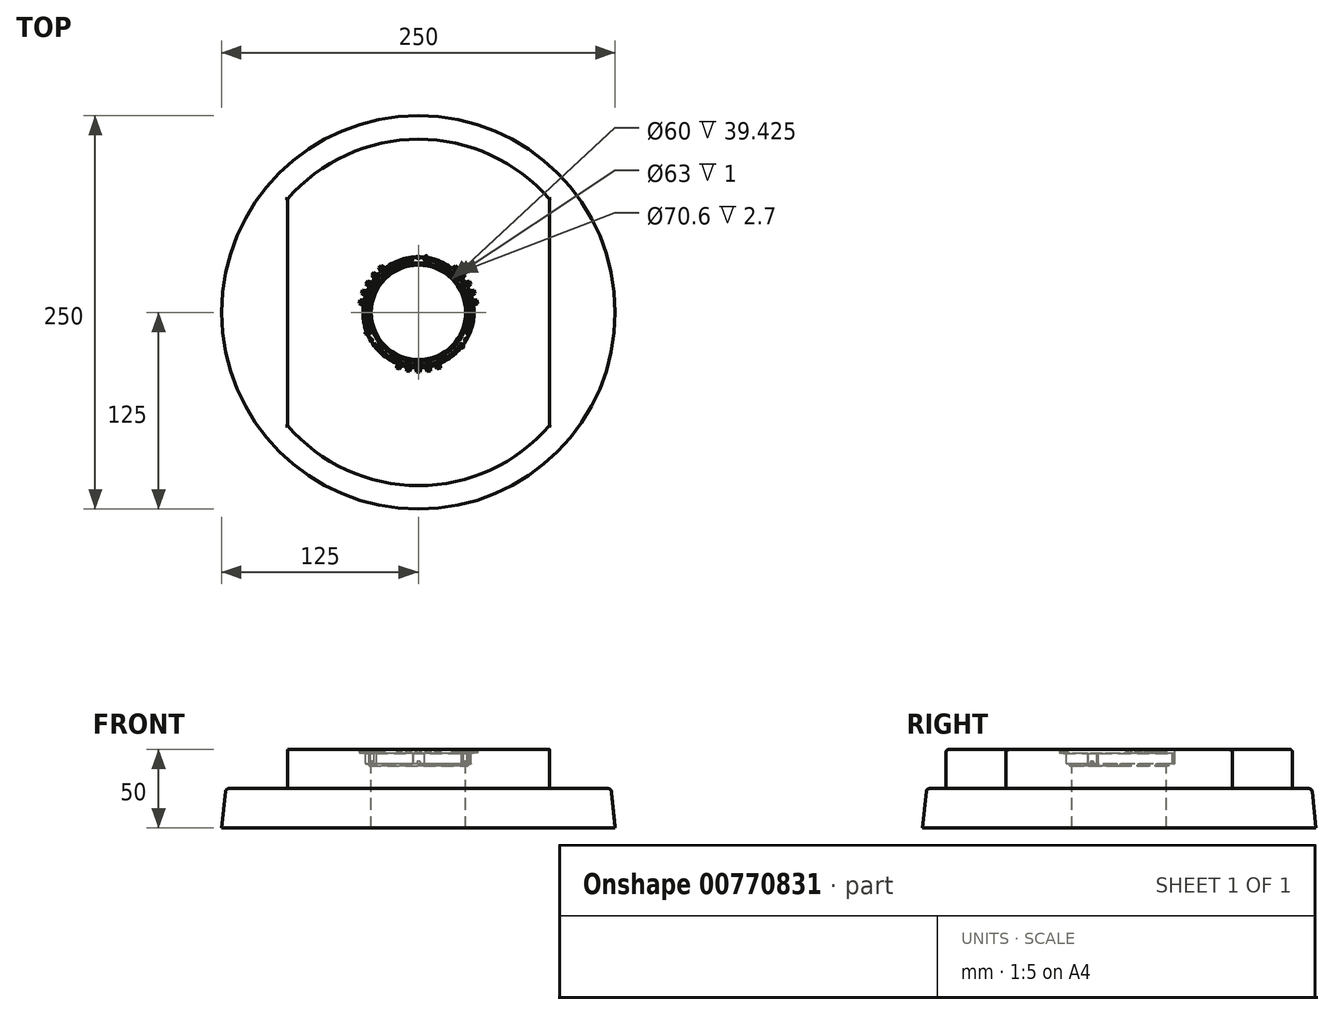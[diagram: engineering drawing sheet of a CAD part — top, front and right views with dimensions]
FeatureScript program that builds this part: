
annotation { "Feature Type Name" : "Feature", "Feature Type Description" : "" }
export const myFeature = defineFeature(function(context is Context, id is Id, definition is map)
    precondition{}
    {
        {
            var Q0;
            Q0=qCreatedBy(makeId("Front.planeOp"),FACE);
            var sketch = newSketch(context, id + "F0", { "sketchPlane" : qUnion([Q0])});
            skLineSegment(sketch, "E0", {"start": v(0, 117.97) * mm, "end": v(0, 0) * mm, "construction": true});
            skLineSegment(sketch, "E1", {"start": v(0, 0) * mm, "end": v(-164.87, 0) * mm, "construction": true});
            skLineSegment(sketch, "E2.bottom", {"start": v(-125, 0) * mm, "end": v(-30, 0) * mm});
            skLineSegment(sketch, "E2.top", {"start": v(-110, 50) * mm, "end": v(-37.95, 50) * mm});
            skLineSegment(sketch, "E2.right", {"start": v(0, 0) * mm, "end": v(0, 50) * mm});
            skLineSegment(sketch, "E3", {"start": v(-125, 25) * mm, "end": v(-110, 25) * mm});
            skLineSegment(sketch, "E4", {"start": v(-110, 25) * mm, "end": v(-110, 50) * mm});
            skLineSegment(sketch, "E5", {"start": v(-30, 39.43) * mm, "end": v(-30, 0) * mm});
            skLineSegment(sketch, "E6", {"start": v(-33.5, 46.85) * mm, "end": v(-33.5, 40.73) * mm});
            skLineSegment(sketch, "E7", {"start": v(-33.5, 40.73) * mm, "end": v(-31.5, 40.73) * mm});
            skLineSegment(sketch, "E8", {"start": v(-31.5, 40.73) * mm, "end": v(-31.5, 39.43) * mm});
            skLineSegment(sketch, "E9", {"start": v(-31.5, 39.43) * mm, "end": v(-30, 39.43) * mm});
            skPoint(sketch, "E10.orphan", {"position": v(-30, 50) * mm});
            skLineSegment(sketch, "E11", {"start": v(-33.5, 46.85) * mm, "end": v(-33.5, 50) * mm});
            skLineSegment(sketch, "E12", {"start": v(-33.5, 50) * mm, "end": v(-37.95, 50) * mm});
            skLineSegment(sketch, "E13", {"start": v(-125, 0) * mm, "end": v(-125, 25) * mm});
            skLineSegment(sketch, "E14", {"start": v(-125, 0) * mm, "end": v(-122.32, 25) * mm});
            skSolve(sketch);
        }
        {
            var Q0;
            Q0=makeQuery(id+"F0.imprint","IMPRINT",FACE,{"disambiguationData":[TD([[makeQuery(id+"F0.imprint","IMPRINT",EDGE,{"derivedFrom":sQuery(id+"F0.wireOp",EDGE,"E2.bottom")}),1.0]])]});
            var Q1;
            Q1=sQuery(id+"F0.wireOp",EDGE,"E0");
            revolve(context, id + "F1", {"surfaceOperationType" : NewSurfaceOperationType.NEW, "entities" : qUnion([Q0]), "axis" : qUnion([Q1]), "revolveType" : RevolveType.FULL});
        }
        {
            var Q0;
            Q0=makeQuery(id+"F1.opRevolve","SWEPT_FACE",FACE,{"disambiguationData":[OSD([sQuery(id+"F0.wireOp",EDGE,"E2.top"),sQuery(id+"F0.wireOp",EDGE,"E12")])]});
            var sketch = newSketch(context, id + "F2", { "sketchPlane" : qUnion([Q0])});
            skLineSegment(sketch, "E15.bottom", {"start": v(-83.23, 71.92) * mm, "end": v(83.23, 71.92) * mm});
            skLineSegment(sketch, "E15.top", {"start": v(-83.23, -71.92) * mm, "end": v(83.23, -71.92) * mm});
            skLineSegment(sketch, "E15.left", {"start": v(-83.23, 71.92) * mm, "end": v(-83.23, -71.92) * mm});
            skLineSegment(sketch, "E15.right", {"start": v(83.23, 71.92) * mm, "end": v(83.23, -71.92) * mm});
            skPoint(sketch, "E15.middle", {"position": v(0, 0) * mm});
            skCircle(sketch, "E16", {"center": v(0, 0) * mm, "radius": 110 * mm});
            skSolve(sketch);
        }
        {
            var Q0;
            {var subQ0=sQuery(id+"F2.wireOp",EDGE,"E15.right");Q0=makeQuery(id+"F2.imprint","IMPRINT",FACE,{"disambiguationData":[TD([[makeQuery(id+"F2.imprint","IMPRINT",EDGE,{"derivedFrom":subQ0}),1.0]])]});}
            var Q1;
            {var subQ0=sQuery(id+"F2.wireOp",EDGE,"E15.left");Q1=makeQuery(id+"F2.imprint","IMPRINT",FACE,{"disambiguationData":[TD([[makeQuery(id+"F2.imprint","IMPRINT",EDGE,{"derivedFrom":subQ0}),-1.0]])]});}
            extrude(context, id + "F3", {"entities" : qUnion([Q0, Q1]), "operationType" : NewBodyOperationType.REMOVE, "oppositeDirection" : true, "depth" : 25 * mm, "offsetDistance" : 25 * mm});
        }
        {
            var Q0;
            Q0=makeQuery(id+"F3.boolean.opBoolean","SPLIT",EDGE,{"disambiguationData":[OD(1.0)],"derivedFrom":makeQuery(id+"F1.opRevolve","SWEPT_EDGE",EDGE,{"disambiguationData":[OSD([sQuery(id+"F0.wireOp",EDGE,"E2.top"),sQuery(id+"F0.wireOp",EDGE,"E4")])]})});
            var Q1;
            Q1=makeQuery(id+"F3.boolean.opBoolean","COPY",EDGE,{"derivedFrom":makeQuery(id+"F3.opExtrude","CAP_EDGE",EDGE,{"disambiguationData":[OSD([sQuery(id+"F2.wireOp",EDGE,"E15.left")])],"isStart":true})});
            var Q2;
            Q2=makeQuery(id+"F3.boolean.opBoolean","SPLIT",EDGE,{"disambiguationData":[OD(0.0)],"derivedFrom":makeQuery(id+"F1.opRevolve","SWEPT_EDGE",EDGE,{"disambiguationData":[OSD([sQuery(id+"F0.wireOp",EDGE,"E2.top"),sQuery(id+"F0.wireOp",EDGE,"E4")])]})});
            var Q3;
            Q3=makeQuery(id+"F3.boolean.opBoolean","COPY",EDGE,{"derivedFrom":makeQuery(id+"F3.opExtrude","CAP_EDGE",EDGE,{"disambiguationData":[OSD([sQuery(id+"F2.wireOp",EDGE,"E15.right")])],"isStart":true})});
            var Q4;
            Q4=makeQuery(id+"F1.opRevolve","SWEPT_EDGE",EDGE,{"disambiguationData":[OSD([sQuery(id+"F0.wireOp",EDGE,"E3"),sQuery(id+"F0.wireOp",EDGE,"E14")])]});
            fillet(context, id + "F4", {"entities" : qUnion([Q0, Q1, Q2, Q3, Q4]), "radius" : 2 * mm, "tangentPropagation" : true, "allowEdgeOverflow" : false});
        }
        {
            var Q0;
            Q0=makeQuery(id+"F3.boolean.opBoolean","COPY",EDGE,{"derivedFrom":makeQuery(id+"F3.opExtrude","CAP_EDGE",EDGE,{"disambiguationData":[OSD([sQuery(id+"F2.wireOp",EDGE,"E15.left")])],"isStart":false})});
            var Q1;
            Q1=makeQuery(id+"F3.boolean.opBoolean","COPY",EDGE,{"derivedFrom":makeQuery(id+"F3.opExtrude","CAP_EDGE",EDGE,{"disambiguationData":[OSD([sQuery(id+"F2.wireOp",EDGE,"E15.right")])],"isStart":false})});
            var Q2;
            Q2=makeQuery(id+"F3.boolean.opBoolean","SPLIT",EDGE,{"disambiguationData":[OD(0.0)],"derivedFrom":makeQuery(id+"F1.opRevolve","SWEPT_EDGE",EDGE,{"disambiguationData":[OSD([sQuery(id+"F0.wireOp",EDGE,"E3"),sQuery(id+"F0.wireOp",EDGE,"E4")])]})});
            var Q3;
            Q3=makeQuery(id+"F3.boolean.opBoolean","SPLIT",EDGE,{"disambiguationData":[OD(1.0)],"derivedFrom":makeQuery(id+"F1.opRevolve","SWEPT_EDGE",EDGE,{"disambiguationData":[OSD([sQuery(id+"F0.wireOp",EDGE,"E3"),sQuery(id+"F0.wireOp",EDGE,"E4")])]})});
            fillet(context, id + "F5", {"entities" : qUnion([Q0, Q1, Q2, Q3]), "radius" : 1 * mm, "tangentPropagation" : true, "allowEdgeOverflow" : false});
        }
        {
            var Q0;
            Q0=makeQuery(id+"F1.opRevolve","SWEPT_EDGE",EDGE,{"disambiguationData":[OSD([sQuery(id+"F0.wireOp",EDGE,"E8"),sQuery(id+"F0.wireOp",EDGE,"E9")])]});
            fillet(context, id + "F6", {"entities" : qUnion([Q0]), "radius" : .3 * mm, "tangentPropagation" : true, "allowEdgeOverflow" : false});
        }
        {
            var Q0;
            Q0=qCreatedBy(makeId("Front.planeOp"),FACE);
            cPlane(context, id + "F7", {"entities" : qUnion([Q0]), "cplaneType" : CPlaneType.OFFSET, "offset" : 30 * mm, "width" : 150 * mm, "height" : 150 * mm});
        }
        {
            var Q0;
            Q0=qCreatedBy(makeId("Front.planeOp"),FACE);
            cPlane(context, id + "F8", {"entities" : qUnion([Q0]), "cplaneType" : CPlaneType.OFFSET, "offset" : 38 * mm, "width" : 150 * mm, "height" : 150 * mm});
        }
        {
            var Q0;
            Q0=qCreatedBy(id+"F8.planeOp",FACE);
            var sketch = newSketch(context, id + "F9", { "sketchPlane" : qUnion([Q0])});
            skPoint(sketch, "E17.start.orphan", {"position": v(0, 93.3) * mm});
            skLineSegment(sketch, "E18", {"start": v(0, 50) * mm, "end": v(-1.1, 50) * mm});
            skLineSegment(sketch, "E19", {"start": v(0, 100.28) * mm, "end": v(0, 50) * mm, "construction": true});
            skLineSegment(sketch, "E20.MirrorCS", {"start": v(0, 50) * mm, "end": v(1.1, 50) * mm});
            skPoint(sketch, "E21", {"position": v(0, 47.8) * mm});
            skLineSegment(sketch, "E22", {"start": v(-1.1, 50) * mm, "end": v(-1.1, 48.2) * mm});
            skLineSegment(sketch, "E23", {"start": v(-1.1, 48.2) * mm, "end": v(0, 47.8) * mm});
            skLineSegment(sketch, "E24.MirrorCS", {"start": v(1.1, 50) * mm, "end": v(1.1, 48.2) * mm});
            skLineSegment(sketch, "E25.MirrorCS", {"start": v(1.1, 48.2) * mm, "end": v(0, 47.8) * mm});
            skLineSegment(sketch, "E26.trimOffspring", {"start": v(0, 47.8) * mm, "end": v(0, 0) * mm, "construction": true});
            skSolve(sketch);
        }
        {
            var Q0;
            Q0=qCreatedBy(id+"F7.planeOp",FACE);
            var sketch = newSketch(context, id + "F10", { "sketchPlane" : qUnion([Q0])});
            skLineSegment(sketch, "E27", {"start": v(0, 52.95) * mm, "end": v(0, 0) * mm, "construction": true});
            skLineSegment(sketch, "E28", {"start": v(-3, 50) * mm, "end": v(0, 50) * mm});
            skLineSegment(sketch, "E29.MirrorCS", {"start": v(3, 50) * mm, "end": v(0, 50) * mm});
            skLineSegment(sketch, "E30", {"start": v(-3, 50) * mm, "end": v(-3, 48.2) * mm});
            skPoint(sketch, "E31", {"position": v(0, 47.2) * mm});
            skLineSegment(sketch, "E32", {"start": v(-3, 48.2) * mm, "end": v(0, 47.2) * mm});
            skLineSegment(sketch, "E33.MirrorCS", {"start": v(3, 50) * mm, "end": v(3, 48.2) * mm});
            skLineSegment(sketch, "E34.MirrorCS", {"start": v(3, 48.2) * mm, "end": v(0, 47.2) * mm});
            skSolve(sketch);
        }
        {
            var Q0;
            Q0=makeQuery(id+"F9.imprint","IMPRINT",FACE,{"disambiguationData":[TD([[makeQuery(id+"F9.imprint","IMPRINT",EDGE,{"derivedFrom":sQuery(id+"F9.wireOp",EDGE,"E18")}),1.0]])]});
            var Q1;
            Q1=makeQuery(id+"F10.imprint","IMPRINT",FACE,{"disambiguationData":[TD([[makeQuery(id+"F10.imprint","IMPRINT",EDGE,{"derivedFrom":sQuery(id+"F10.wireOp",EDGE,"E28")}),-1.0]])]});
            loft(context, id + "F11", {"operationType" : NewBodyOperationType.REMOVE, "sheetProfilesArray" : [{ "sheetProfileEntities" : qUnion([Q0]) }, { "sheetProfileEntities" : qUnion([Q1]) }]});
        }
        {
            var Q0;
            Q0=makeQuery(id+"F11.boolean.opBoolean","COPY",FACE,{"derivedFrom":makeQuery(id+"F11.opLoft","SWEPT_FACE",FACE,{"disambiguationData":[OSD([sQuery(id+"F9.wireOp",EDGE,"E22"),sQuery(id+"F9.wireOp",EDGE,"E23"),sQuery(id+"F9.wireOp",EDGE,"E25.MirrorCS"),sQuery(id+"F10.wireOp",EDGE,"E30"),sQuery(id+"F10.wireOp",EDGE,"E32"),sQuery(id+"F10.wireOp",EDGE,"E34.MirrorCS")])]})});
            var Q1;
            Q1=makeQuery(id+"F11.boolean.opBoolean","COPY",FACE,{"derivedFrom":makeQuery(id+"F11.opLoft","SWEPT_FACE",FACE,{"disambiguationData":[OSD([sQuery(id+"F9.wireOp",EDGE,"E18"),sQuery(id+"F9.wireOp",EDGE,"E22"),sQuery(id+"F9.wireOp",EDGE,"E23"),sQuery(id+"F10.wireOp",EDGE,"E28"),sQuery(id+"F10.wireOp",EDGE,"E30"),sQuery(id+"F10.wireOp",EDGE,"E32")])]})});
            var Q2;
            Q2=makeQuery(id+"F11.boolean.opBoolean","COPY",FACE,{"derivedFrom":makeQuery(id+"F11.opLoft","SWEPT_FACE",FACE,{"disambiguationData":[OSD([sQuery(id+"F9.wireOp",EDGE,"E23"),sQuery(id+"F9.wireOp",EDGE,"E24.MirrorCS"),sQuery(id+"F9.wireOp",EDGE,"E25.MirrorCS"),sQuery(id+"F10.wireOp",EDGE,"E32"),sQuery(id+"F10.wireOp",EDGE,"E33.MirrorCS"),sQuery(id+"F10.wireOp",EDGE,"E34.MirrorCS")])]})});
            var Q3;
            Q3=makeQuery(id+"F11.boolean.opBoolean","COPY",FACE,{"derivedFrom":makeQuery(id+"F11.opLoft","SWEPT_FACE",FACE,{"disambiguationData":[OSD([sQuery(id+"F9.wireOp",EDGE,"E24.MirrorCS"),sQuery(id+"F9.wireOp",EDGE,"E20.MirrorCS"),sQuery(id+"F9.wireOp",EDGE,"E25.MirrorCS"),sQuery(id+"F10.wireOp",EDGE,"E29.MirrorCS"),sQuery(id+"F10.wireOp",EDGE,"E33.MirrorCS"),sQuery(id+"F10.wireOp",EDGE,"E34.MirrorCS")])]})});
            var Q4;
            Q4=makeQuery(id+"F11.boolean.opBoolean","COPY",FACE,{"derivedFrom":makeQuery(id+"F11.opLoft","CAP_FACE",FACE,{"disambiguationData":[OSD([makeQuery(id+"F9.imprint","IMPRINT",FACE,{"disambiguationData":[TD([[makeQuery(id+"F9.imprint","IMPRINT",EDGE,{"derivedFrom":sQuery(id+"F9.wireOp",EDGE,"E18")}),1.0]])]})])],"isStart":true})});
            var Q5;
            Q5=makeQuery(id+"F1.opRevolve","SWEPT_FACE",FACE,{"disambiguationData":[OSD([sQuery(id+"F0.wireOp",EDGE,"E6"),sQuery(id+"F0.wireOp",EDGE,"E11")])]});
            circularPattern(context, id + "F12", {"patternType" : PatternType.FACE, "faces" : qUnion([Q0, Q1, Q2, Q3, Q4]), "axis" : qUnion([Q5]), "angle" : 20 * degree, "instanceCount" : 3, "equalSpace" : true});
        }
        {
            var Q0;
            Q0=makeQuery(id+"F11.boolean.opBoolean","COPY",FACE,{"derivedFrom":makeQuery(id+"F11.opLoft","SWEPT_FACE",FACE,{"disambiguationData":[OSD([sQuery(id+"F9.wireOp",EDGE,"E22"),sQuery(id+"F9.wireOp",EDGE,"E23"),sQuery(id+"F9.wireOp",EDGE,"E25.MirrorCS"),sQuery(id+"F10.wireOp",EDGE,"E30"),sQuery(id+"F10.wireOp",EDGE,"E32"),sQuery(id+"F10.wireOp",EDGE,"E34.MirrorCS")])]})});
            var Q1;
            Q1=makeQuery(id+"F11.boolean.opBoolean","COPY",FACE,{"derivedFrom":makeQuery(id+"F11.opLoft","SWEPT_FACE",FACE,{"disambiguationData":[OSD([sQuery(id+"F9.wireOp",EDGE,"E18"),sQuery(id+"F9.wireOp",EDGE,"E22"),sQuery(id+"F9.wireOp",EDGE,"E23"),sQuery(id+"F10.wireOp",EDGE,"E28"),sQuery(id+"F10.wireOp",EDGE,"E30"),sQuery(id+"F10.wireOp",EDGE,"E32")])]})});
            var Q2;
            Q2=makeQuery(id+"F11.boolean.opBoolean","COPY",FACE,{"derivedFrom":makeQuery(id+"F11.opLoft","SWEPT_FACE",FACE,{"disambiguationData":[OSD([sQuery(id+"F9.wireOp",EDGE,"E23"),sQuery(id+"F9.wireOp",EDGE,"E24.MirrorCS"),sQuery(id+"F9.wireOp",EDGE,"E25.MirrorCS"),sQuery(id+"F10.wireOp",EDGE,"E32"),sQuery(id+"F10.wireOp",EDGE,"E33.MirrorCS"),sQuery(id+"F10.wireOp",EDGE,"E34.MirrorCS")])]})});
            var Q3;
            Q3=makeQuery(id+"F11.boolean.opBoolean","COPY",FACE,{"derivedFrom":makeQuery(id+"F11.opLoft","SWEPT_FACE",FACE,{"disambiguationData":[OSD([sQuery(id+"F9.wireOp",EDGE,"E24.MirrorCS"),sQuery(id+"F9.wireOp",EDGE,"E20.MirrorCS"),sQuery(id+"F9.wireOp",EDGE,"E25.MirrorCS"),sQuery(id+"F10.wireOp",EDGE,"E29.MirrorCS"),sQuery(id+"F10.wireOp",EDGE,"E33.MirrorCS"),sQuery(id+"F10.wireOp",EDGE,"E34.MirrorCS")])]})});
            var Q4;
            Q4=makeQuery(id+"F11.boolean.opBoolean","COPY",FACE,{"derivedFrom":makeQuery(id+"F11.opLoft","CAP_FACE",FACE,{"disambiguationData":[OSD([makeQuery(id+"F9.imprint","IMPRINT",FACE,{"disambiguationData":[TD([[makeQuery(id+"F9.imprint","IMPRINT",EDGE,{"derivedFrom":sQuery(id+"F9.wireOp",EDGE,"E18")}),1.0]])]})])],"isStart":true})});
            var Q5;
            Q5=makeQuery(id+"F1.opRevolve","SWEPT_FACE",FACE,{"disambiguationData":[OSD([sQuery(id+"F0.wireOp",EDGE,"E6"),sQuery(id+"F0.wireOp",EDGE,"E11")])]});
            circularPattern(context, id + "F13", {"patternType" : PatternType.FACE, "faces" : qUnion([Q0, Q1, Q2, Q3, Q4]), "axis" : qUnion([Q5]), "angle" : 20 * degree, "instanceCount" : 3, "oppositeDirection" : true, "equalSpace" : true});
        }
        {
            var Q0;
            Q0=makeQuery(id+"F12.opPattern","COPY",FACE,{"derivedFrom":makeQuery(id+"F11.boolean.opBoolean","COPY",FACE,{"derivedFrom":makeQuery(id+"F11.opLoft","SWEPT_FACE",FACE,{"disambiguationData":[OSD([sQuery(id+"F9.wireOp",EDGE,"E22"),sQuery(id+"F9.wireOp",EDGE,"E23"),sQuery(id+"F9.wireOp",EDGE,"E25.MirrorCS"),sQuery(id+"F10.wireOp",EDGE,"E30"),sQuery(id+"F10.wireOp",EDGE,"E32"),sQuery(id+"F10.wireOp",EDGE,"E34.MirrorCS")])]})}),"instanceName":"2"});
            var Q1;
            Q1=makeQuery(id+"F12.opPattern","COPY",FACE,{"derivedFrom":makeQuery(id+"F11.boolean.opBoolean","COPY",FACE,{"derivedFrom":makeQuery(id+"F11.opLoft","SWEPT_FACE",FACE,{"disambiguationData":[OSD([sQuery(id+"F9.wireOp",EDGE,"E23"),sQuery(id+"F9.wireOp",EDGE,"E24.MirrorCS"),sQuery(id+"F9.wireOp",EDGE,"E25.MirrorCS"),sQuery(id+"F10.wireOp",EDGE,"E32"),sQuery(id+"F10.wireOp",EDGE,"E33.MirrorCS"),sQuery(id+"F10.wireOp",EDGE,"E34.MirrorCS")])]})}),"instanceName":"2"});
            var Q2;
            Q2=makeQuery(id+"F12.opPattern","COPY",FACE,{"derivedFrom":makeQuery(id+"F11.boolean.opBoolean","COPY",FACE,{"derivedFrom":makeQuery(id+"F11.opLoft","SWEPT_FACE",FACE,{"disambiguationData":[OSD([sQuery(id+"F9.wireOp",EDGE,"E18"),sQuery(id+"F9.wireOp",EDGE,"E22"),sQuery(id+"F9.wireOp",EDGE,"E23"),sQuery(id+"F10.wireOp",EDGE,"E28"),sQuery(id+"F10.wireOp",EDGE,"E30"),sQuery(id+"F10.wireOp",EDGE,"E32")])]})}),"instanceName":"2"});
            var Q3;
            Q3=makeQuery(id+"F12.opPattern","COPY",FACE,{"derivedFrom":makeQuery(id+"F11.boolean.opBoolean","COPY",FACE,{"derivedFrom":makeQuery(id+"F11.opLoft","CAP_FACE",FACE,{"disambiguationData":[OSD([makeQuery(id+"F9.imprint","IMPRINT",FACE,{"disambiguationData":[TD([[makeQuery(id+"F9.imprint","IMPRINT",EDGE,{"derivedFrom":sQuery(id+"F9.wireOp",EDGE,"E18")}),1.0]])]})])],"isStart":true})}),"instanceName":"2"});
            var Q4;
            Q4=makeQuery(id+"F12.opPattern","COPY",FACE,{"derivedFrom":makeQuery(id+"F11.boolean.opBoolean","COPY",FACE,{"derivedFrom":makeQuery(id+"F11.opLoft","SWEPT_FACE",FACE,{"disambiguationData":[OSD([sQuery(id+"F9.wireOp",EDGE,"E24.MirrorCS"),sQuery(id+"F9.wireOp",EDGE,"E20.MirrorCS"),sQuery(id+"F9.wireOp",EDGE,"E25.MirrorCS"),sQuery(id+"F10.wireOp",EDGE,"E29.MirrorCS"),sQuery(id+"F10.wireOp",EDGE,"E33.MirrorCS"),sQuery(id+"F10.wireOp",EDGE,"E34.MirrorCS")])]})}),"instanceName":"2"});
            var Q5;
            Q5=makeQuery(id+"F12.opPattern","COPY",FACE,{"derivedFrom":makeQuery(id+"F11.boolean.opBoolean","COPY",FACE,{"derivedFrom":makeQuery(id+"F11.opLoft","SWEPT_FACE",FACE,{"disambiguationData":[OSD([sQuery(id+"F9.wireOp",EDGE,"E22"),sQuery(id+"F9.wireOp",EDGE,"E23"),sQuery(id+"F9.wireOp",EDGE,"E25.MirrorCS"),sQuery(id+"F10.wireOp",EDGE,"E30"),sQuery(id+"F10.wireOp",EDGE,"E32"),sQuery(id+"F10.wireOp",EDGE,"E34.MirrorCS")])]})}),"instanceName":"1"});
            var Q6;
            Q6=makeQuery(id+"F12.opPattern","COPY",FACE,{"derivedFrom":makeQuery(id+"F11.boolean.opBoolean","COPY",FACE,{"derivedFrom":makeQuery(id+"F11.opLoft","SWEPT_FACE",FACE,{"disambiguationData":[OSD([sQuery(id+"F9.wireOp",EDGE,"E23"),sQuery(id+"F9.wireOp",EDGE,"E24.MirrorCS"),sQuery(id+"F9.wireOp",EDGE,"E25.MirrorCS"),sQuery(id+"F10.wireOp",EDGE,"E32"),sQuery(id+"F10.wireOp",EDGE,"E33.MirrorCS"),sQuery(id+"F10.wireOp",EDGE,"E34.MirrorCS")])]})}),"instanceName":"1"});
            var Q7;
            Q7=makeQuery(id+"F12.opPattern","COPY",FACE,{"derivedFrom":makeQuery(id+"F11.boolean.opBoolean","COPY",FACE,{"derivedFrom":makeQuery(id+"F11.opLoft","SWEPT_FACE",FACE,{"disambiguationData":[OSD([sQuery(id+"F9.wireOp",EDGE,"E18"),sQuery(id+"F9.wireOp",EDGE,"E22"),sQuery(id+"F9.wireOp",EDGE,"E23"),sQuery(id+"F10.wireOp",EDGE,"E28"),sQuery(id+"F10.wireOp",EDGE,"E30"),sQuery(id+"F10.wireOp",EDGE,"E32")])]})}),"instanceName":"1"});
            var Q8;
            Q8=makeQuery(id+"F12.opPattern","COPY",FACE,{"derivedFrom":makeQuery(id+"F11.boolean.opBoolean","COPY",FACE,{"derivedFrom":makeQuery(id+"F11.opLoft","CAP_FACE",FACE,{"disambiguationData":[OSD([makeQuery(id+"F9.imprint","IMPRINT",FACE,{"disambiguationData":[TD([[makeQuery(id+"F9.imprint","IMPRINT",EDGE,{"derivedFrom":sQuery(id+"F9.wireOp",EDGE,"E18")}),1.0]])]})])],"isStart":true})}),"instanceName":"1"});
            var Q9;
            Q9=makeQuery(id+"F12.opPattern","COPY",FACE,{"derivedFrom":makeQuery(id+"F11.boolean.opBoolean","COPY",FACE,{"derivedFrom":makeQuery(id+"F11.opLoft","SWEPT_FACE",FACE,{"disambiguationData":[OSD([sQuery(id+"F9.wireOp",EDGE,"E24.MirrorCS"),sQuery(id+"F9.wireOp",EDGE,"E20.MirrorCS"),sQuery(id+"F9.wireOp",EDGE,"E25.MirrorCS"),sQuery(id+"F10.wireOp",EDGE,"E29.MirrorCS"),sQuery(id+"F10.wireOp",EDGE,"E33.MirrorCS"),sQuery(id+"F10.wireOp",EDGE,"E34.MirrorCS")])]})}),"instanceName":"1"});
            var Q10;
            Q10=makeQuery(id+"F11.boolean.opBoolean","COPY",FACE,{"derivedFrom":makeQuery(id+"F11.opLoft","SWEPT_FACE",FACE,{"disambiguationData":[OSD([sQuery(id+"F9.wireOp",EDGE,"E23"),sQuery(id+"F9.wireOp",EDGE,"E24.MirrorCS"),sQuery(id+"F9.wireOp",EDGE,"E25.MirrorCS"),sQuery(id+"F10.wireOp",EDGE,"E32"),sQuery(id+"F10.wireOp",EDGE,"E33.MirrorCS"),sQuery(id+"F10.wireOp",EDGE,"E34.MirrorCS")])]})});
            var Q11;
            Q11=makeQuery(id+"F11.boolean.opBoolean","COPY",FACE,{"derivedFrom":makeQuery(id+"F11.opLoft","SWEPT_FACE",FACE,{"disambiguationData":[OSD([sQuery(id+"F9.wireOp",EDGE,"E22"),sQuery(id+"F9.wireOp",EDGE,"E23"),sQuery(id+"F9.wireOp",EDGE,"E25.MirrorCS"),sQuery(id+"F10.wireOp",EDGE,"E30"),sQuery(id+"F10.wireOp",EDGE,"E32"),sQuery(id+"F10.wireOp",EDGE,"E34.MirrorCS")])]})});
            var Q12;
            Q12=makeQuery(id+"F11.boolean.opBoolean","COPY",FACE,{"derivedFrom":makeQuery(id+"F11.opLoft","CAP_FACE",FACE,{"disambiguationData":[OSD([makeQuery(id+"F9.imprint","IMPRINT",FACE,{"disambiguationData":[TD([[makeQuery(id+"F9.imprint","IMPRINT",EDGE,{"derivedFrom":sQuery(id+"F9.wireOp",EDGE,"E18")}),1.0]])]})])],"isStart":true})});
            var Q13;
            Q13=makeQuery(id+"F11.boolean.opBoolean","COPY",FACE,{"derivedFrom":makeQuery(id+"F11.opLoft","SWEPT_FACE",FACE,{"disambiguationData":[OSD([sQuery(id+"F9.wireOp",EDGE,"E18"),sQuery(id+"F9.wireOp",EDGE,"E22"),sQuery(id+"F9.wireOp",EDGE,"E23"),sQuery(id+"F10.wireOp",EDGE,"E28"),sQuery(id+"F10.wireOp",EDGE,"E30"),sQuery(id+"F10.wireOp",EDGE,"E32")])]})});
            var Q14;
            Q14=makeQuery(id+"F11.boolean.opBoolean","COPY",FACE,{"derivedFrom":makeQuery(id+"F11.opLoft","SWEPT_FACE",FACE,{"disambiguationData":[OSD([sQuery(id+"F9.wireOp",EDGE,"E24.MirrorCS"),sQuery(id+"F9.wireOp",EDGE,"E20.MirrorCS"),sQuery(id+"F9.wireOp",EDGE,"E25.MirrorCS"),sQuery(id+"F10.wireOp",EDGE,"E29.MirrorCS"),sQuery(id+"F10.wireOp",EDGE,"E33.MirrorCS"),sQuery(id+"F10.wireOp",EDGE,"E34.MirrorCS")])]})});
            var Q15;
            Q15=makeQuery(id+"F13.opPattern","COPY",FACE,{"derivedFrom":makeQuery(id+"F11.boolean.opBoolean","COPY",FACE,{"derivedFrom":makeQuery(id+"F11.opLoft","SWEPT_FACE",FACE,{"disambiguationData":[OSD([sQuery(id+"F9.wireOp",EDGE,"E23"),sQuery(id+"F9.wireOp",EDGE,"E24.MirrorCS"),sQuery(id+"F9.wireOp",EDGE,"E25.MirrorCS"),sQuery(id+"F10.wireOp",EDGE,"E32"),sQuery(id+"F10.wireOp",EDGE,"E33.MirrorCS"),sQuery(id+"F10.wireOp",EDGE,"E34.MirrorCS")])]})}),"instanceName":"1"});
            var Q16;
            Q16=makeQuery(id+"F13.opPattern","COPY",FACE,{"derivedFrom":makeQuery(id+"F11.boolean.opBoolean","COPY",FACE,{"derivedFrom":makeQuery(id+"F11.opLoft","SWEPT_FACE",FACE,{"disambiguationData":[OSD([sQuery(id+"F9.wireOp",EDGE,"E22"),sQuery(id+"F9.wireOp",EDGE,"E23"),sQuery(id+"F9.wireOp",EDGE,"E25.MirrorCS"),sQuery(id+"F10.wireOp",EDGE,"E30"),sQuery(id+"F10.wireOp",EDGE,"E32"),sQuery(id+"F10.wireOp",EDGE,"E34.MirrorCS")])]})}),"instanceName":"1"});
            var Q17;
            Q17=makeQuery(id+"F13.opPattern","COPY",FACE,{"derivedFrom":makeQuery(id+"F11.boolean.opBoolean","COPY",FACE,{"derivedFrom":makeQuery(id+"F11.opLoft","SWEPT_FACE",FACE,{"disambiguationData":[OSD([sQuery(id+"F9.wireOp",EDGE,"E18"),sQuery(id+"F9.wireOp",EDGE,"E22"),sQuery(id+"F9.wireOp",EDGE,"E23"),sQuery(id+"F10.wireOp",EDGE,"E28"),sQuery(id+"F10.wireOp",EDGE,"E30"),sQuery(id+"F10.wireOp",EDGE,"E32")])]})}),"instanceName":"1"});
            var Q18;
            Q18=makeQuery(id+"F13.opPattern","COPY",FACE,{"derivedFrom":makeQuery(id+"F11.boolean.opBoolean","COPY",FACE,{"derivedFrom":makeQuery(id+"F11.opLoft","CAP_FACE",FACE,{"disambiguationData":[OSD([makeQuery(id+"F9.imprint","IMPRINT",FACE,{"disambiguationData":[TD([[makeQuery(id+"F9.imprint","IMPRINT",EDGE,{"derivedFrom":sQuery(id+"F9.wireOp",EDGE,"E18")}),1.0]])]})])],"isStart":true})}),"instanceName":"1"});
            var Q19;
            Q19=makeQuery(id+"F13.opPattern","COPY",FACE,{"derivedFrom":makeQuery(id+"F11.boolean.opBoolean","COPY",FACE,{"derivedFrom":makeQuery(id+"F11.opLoft","SWEPT_FACE",FACE,{"disambiguationData":[OSD([sQuery(id+"F9.wireOp",EDGE,"E24.MirrorCS"),sQuery(id+"F9.wireOp",EDGE,"E20.MirrorCS"),sQuery(id+"F9.wireOp",EDGE,"E25.MirrorCS"),sQuery(id+"F10.wireOp",EDGE,"E29.MirrorCS"),sQuery(id+"F10.wireOp",EDGE,"E33.MirrorCS"),sQuery(id+"F10.wireOp",EDGE,"E34.MirrorCS")])]})}),"instanceName":"1"});
            var Q20;
            Q20=makeQuery(id+"F13.opPattern","COPY",FACE,{"derivedFrom":makeQuery(id+"F11.boolean.opBoolean","COPY",FACE,{"derivedFrom":makeQuery(id+"F11.opLoft","SWEPT_FACE",FACE,{"disambiguationData":[OSD([sQuery(id+"F9.wireOp",EDGE,"E22"),sQuery(id+"F9.wireOp",EDGE,"E23"),sQuery(id+"F9.wireOp",EDGE,"E25.MirrorCS"),sQuery(id+"F10.wireOp",EDGE,"E30"),sQuery(id+"F10.wireOp",EDGE,"E32"),sQuery(id+"F10.wireOp",EDGE,"E34.MirrorCS")])]})}),"instanceName":"2"});
            var Q21;
            Q21=makeQuery(id+"F13.opPattern","COPY",FACE,{"derivedFrom":makeQuery(id+"F11.boolean.opBoolean","COPY",FACE,{"derivedFrom":makeQuery(id+"F11.opLoft","SWEPT_FACE",FACE,{"disambiguationData":[OSD([sQuery(id+"F9.wireOp",EDGE,"E23"),sQuery(id+"F9.wireOp",EDGE,"E24.MirrorCS"),sQuery(id+"F9.wireOp",EDGE,"E25.MirrorCS"),sQuery(id+"F10.wireOp",EDGE,"E32"),sQuery(id+"F10.wireOp",EDGE,"E33.MirrorCS"),sQuery(id+"F10.wireOp",EDGE,"E34.MirrorCS")])]})}),"instanceName":"2"});
            var Q22;
            Q22=makeQuery(id+"F13.opPattern","COPY",FACE,{"derivedFrom":makeQuery(id+"F11.boolean.opBoolean","COPY",FACE,{"derivedFrom":makeQuery(id+"F11.opLoft","SWEPT_FACE",FACE,{"disambiguationData":[OSD([sQuery(id+"F9.wireOp",EDGE,"E18"),sQuery(id+"F9.wireOp",EDGE,"E22"),sQuery(id+"F9.wireOp",EDGE,"E23"),sQuery(id+"F10.wireOp",EDGE,"E28"),sQuery(id+"F10.wireOp",EDGE,"E30"),sQuery(id+"F10.wireOp",EDGE,"E32")])]})}),"instanceName":"2"});
            var Q23;
            Q23=makeQuery(id+"F13.opPattern","COPY",FACE,{"derivedFrom":makeQuery(id+"F11.boolean.opBoolean","COPY",FACE,{"derivedFrom":makeQuery(id+"F11.opLoft","CAP_FACE",FACE,{"disambiguationData":[OSD([makeQuery(id+"F9.imprint","IMPRINT",FACE,{"disambiguationData":[TD([[makeQuery(id+"F9.imprint","IMPRINT",EDGE,{"derivedFrom":sQuery(id+"F9.wireOp",EDGE,"E18")}),1.0]])]})])],"isStart":true})}),"instanceName":"2"});
            var Q24;
            Q24=makeQuery(id+"F13.opPattern","COPY",FACE,{"derivedFrom":makeQuery(id+"F11.boolean.opBoolean","COPY",FACE,{"derivedFrom":makeQuery(id+"F11.opLoft","SWEPT_FACE",FACE,{"disambiguationData":[OSD([sQuery(id+"F9.wireOp",EDGE,"E24.MirrorCS"),sQuery(id+"F9.wireOp",EDGE,"E20.MirrorCS"),sQuery(id+"F9.wireOp",EDGE,"E25.MirrorCS"),sQuery(id+"F10.wireOp",EDGE,"E29.MirrorCS"),sQuery(id+"F10.wireOp",EDGE,"E33.MirrorCS"),sQuery(id+"F10.wireOp",EDGE,"E34.MirrorCS")])]})}),"instanceName":"2"});
            var Q25;
            Q25=makeQuery(id+"F1.opRevolve","SWEPT_FACE",FACE,{"disambiguationData":[OSD([sQuery(id+"F0.wireOp",EDGE,"E6"),sQuery(id+"F0.wireOp",EDGE,"E11")])]});
            circularPattern(context, id + "F14", {"patternType" : PatternType.FACE, "faces" : qUnion([Q0, Q1, Q2, Q3, Q4, Q5, Q6, Q7, Q8, Q9, Q10, Q11, Q12, Q13, Q14, Q15, Q16, Q17, Q18, Q19, Q20, Q21, Q22, Q23, Q24]), "axis" : qUnion([Q25]), "angle" : 360 * degree, "instanceCount" : 3, "equalSpace" : true});
        }
        {
            var Q0;
            Q0=makeQuery(id+"F1.opRevolve","SWEPT_FACE",FACE,{"disambiguationData":[OSD([sQuery(id+"F0.wireOp",EDGE,"E2.top"),sQuery(id+"F0.wireOp",EDGE,"E12")])]});
            var sketch = newSketch(context, id + "F15", { "sketchPlane" : qUnion([Q0])});
            skCircle(sketch, "E35", {"center": v(0, 0) * mm, "radius": 33.5 * mm});
            skCircle(sketch, "E36", {"center": v(0, 0) * mm, "radius": 35.3 * mm});
            skLineSegment(sketch, "E37", {"start": v(0, 52.04) * mm, "end": v(0, 0) * mm, "construction": true});
            skLineSegment(sketch, "E38", {"start": v(-3.4, 35.14) * mm, "end": v(-3.63, 33.3) * mm});
            skLineSegment(sketch, "E39.MirrorCS", {"start": v(3.4, 35.14) * mm, "end": v(3.63, 33.3) * mm});
            skLineSegment(sketch, "E40.1.0", {"start": v(-28.73, -20.51) * mm, "end": v(-27.03, -19.8) * mm});
            skLineSegment(sketch, "E40.1.1", {"start": v(-32.13, -14.62) * mm, "end": v(-30.66, -13.5) * mm});
            skLineSegment(sketch, "E40.2.0", {"start": v(32.13, -14.62) * mm, "end": v(30.66, -13.5) * mm});
            skLineSegment(sketch, "E40.2.1", {"start": v(28.73, -20.51) * mm, "end": v(27.03, -19.8) * mm});
            skSolve(sketch);
        }
        {
            var Q0;
            Q0=qSketchRegion(id+"F15",true);
            extrude(context, id + "F16", {"entities" : qUnion([Q0]), "operationType" : NewBodyOperationType.REMOVE, "oppositeDirection" : true, "depth" : 2.7 * mm, "offsetDistance" : 25 * mm});
        }
        {
            var Q0;
            Q0=makeQuery(id+"F1.opRevolve","SWEPT_FACE",FACE,{"disambiguationData":[OSD([sQuery(id+"F0.wireOp",EDGE,"E7")])]});
            var sketch = newSketch(context, id + "F17", { "sketchPlane" : qUnion([Q0])});
            skCircle(sketch, "E41", {"center": v(0, 0) * mm, "radius": 34.9 * mm});
            skCircle(sketch, "E42", {"center": v(0, 0) * mm, "radius": 33.5 * mm});
            skLineSegment(sketch, "E43", {"start": v(0, 42) * mm, "end": v(0, 0) * mm, "construction": true});
            skLineSegment(sketch, "E44", {"start": v(-3.4, 35.14) * mm, "end": v(-3.63, 33.3) * mm});
            skLineSegment(sketch, "E45.MirrorCS", {"start": v(3.4, 35.14) * mm, "end": v(3.63, 33.3) * mm});
            skLineSegment(sketch, "E46.1.0", {"start": v(-28.73, -20.51) * mm, "end": v(-27.03, -19.8) * mm});
            skLineSegment(sketch, "E46.1.1", {"start": v(-32.13, -14.62) * mm, "end": v(-30.66, -13.5) * mm});
            skLineSegment(sketch, "E46.2.0", {"start": v(32.13, -14.62) * mm, "end": v(30.66, -13.5) * mm});
            skLineSegment(sketch, "E46.2.1", {"start": v(28.73, -20.51) * mm, "end": v(27.03, -19.8) * mm});
            skSolve(sketch);
        }
        {
            var Q0;
            {var subQ0=sQuery(id+"F15.wireOp",EDGE,"E38");Q0=makeQuery(id+"F15.imprint","IMPRINT",FACE,{"disambiguationData":[TD([[makeQuery(id+"F15.imprint","IMPRINT",EDGE,{"derivedFrom":subQ0}),1.0]])]});}
            var Q1;
            {var subQ0=sQuery(id+"F15.wireOp",EDGE,"E40.1.0");Q1=makeQuery(id+"F15.imprint","IMPRINT",FACE,{"disambiguationData":[TD([[makeQuery(id+"F15.imprint","IMPRINT",EDGE,{"derivedFrom":subQ0}),1.0]])]});}
            var Q2;
            {var subQ0=sQuery(id+"F15.wireOp",EDGE,"E40.2.0");Q2=makeQuery(id+"F15.imprint","IMPRINT",FACE,{"disambiguationData":[TD([[makeQuery(id+"F15.imprint","IMPRINT",EDGE,{"derivedFrom":subQ0}),1.0]])]});}
            extrude(context, id + "F18", {"entities" : qUnion([Q0, Q1, Q2]), "operationType" : NewBodyOperationType.REMOVE, "depth" : 25 * mm, "offsetDistance" : 25 * mm});
        }
        {
            var Q0;
            {var subQ0=sQuery(id+"F17.wireOp",EDGE,"E44");var subQ1=sQuery(id+"F17.wireOp",EDGE,"E41");var subQ2=makeQuery(id+"F17.imprint","INTERSECT",VERTEX,{"derivedFrom":[subQ1,subQ0]});Q0=makeQuery(id+"F17.imprint","IMPRINT",FACE,{"disambiguationData":[TD([[makeQuery(id+"F17.imprint","IMPRINT",EDGE,{"disambiguationData":[TD([[subQ2,1.0]])],"derivedFrom":subQ1}),1.0]])]});}
            var Q1;
            {var subQ0=sQuery(id+"F17.wireOp",EDGE,"E46.1.1");var subQ1=sQuery(id+"F17.wireOp",EDGE,"E41");var subQ2=makeQuery(id+"F17.imprint","INTERSECT",VERTEX,{"derivedFrom":[subQ1,subQ0]});Q1=makeQuery(id+"F17.imprint","IMPRINT",FACE,{"disambiguationData":[TD([[makeQuery(id+"F17.imprint","IMPRINT",EDGE,{"disambiguationData":[TD([[subQ2,-1.0]])],"derivedFrom":subQ1}),1.0]])]});}
            var Q2;
            {var subQ0=sQuery(id+"F17.wireOp",EDGE,"E46.2.1");var subQ1=sQuery(id+"F17.wireOp",EDGE,"E41");var subQ2=makeQuery(id+"F17.imprint","INTERSECT",VERTEX,{"derivedFrom":[subQ1,subQ0]});Q2=makeQuery(id+"F17.imprint","IMPRINT",FACE,{"disambiguationData":[TD([[makeQuery(id+"F17.imprint","IMPRINT",EDGE,{"disambiguationData":[TD([[subQ2,-1.0]])],"derivedFrom":subQ1}),1.0]])]});}
            extrude(context, id + "F19", {"entities" : qUnion([Q0, Q1, Q2]), "operationType" : NewBodyOperationType.REMOVE, "depth" : 25 * mm, "offsetDistance" : 25 * mm});
        }
        {
            var Q0;
            {var subQ3=sQuery(id+"F17.wireOp",EDGE,"E44");var subQ4=sQuery(id+"F0.wireOp",EDGE,"E7");var subQ5=sQuery(id+"F0.wireOp",EDGE,"E6");Q0=makeQuery(id+"F19.boolean.opBoolean","SPLIT",EDGE,{"disambiguationData":[TD([makeQuery(id+"F19.opExtrude","SWEPT_FACE",FACE,{"disambiguationData":[OSD([subQ3])]})])],"derivedFrom":makeQuery(id+"F1.opRevolve","SWEPT_EDGE",EDGE,{"disambiguationData":[OSD([subQ5,subQ4])]})});}
            var Q1;
            {var subQ2=sQuery(id+"F17.wireOp",EDGE,"E45.MirrorCS");var subQ3=sQuery(id+"F0.wireOp",EDGE,"E7");var subQ5=sQuery(id+"F0.wireOp",EDGE,"E6");Q1=makeQuery(id+"F19.boolean.opBoolean","SPLIT",EDGE,{"disambiguationData":[TD([makeQuery(id+"F19.opExtrude","SWEPT_FACE",FACE,{"disambiguationData":[OSD([subQ2])]})])],"derivedFrom":makeQuery(id+"F1.opRevolve","SWEPT_EDGE",EDGE,{"disambiguationData":[OSD([subQ5,subQ3])]})});}
            var Q2;
            {var subQ0=sQuery(id+"F17.wireOp",EDGE,"E46.1.0");var subQ3=sQuery(id+"F0.wireOp",EDGE,"E7");var subQ5=sQuery(id+"F0.wireOp",EDGE,"E6");Q2=makeQuery(id+"F19.boolean.opBoolean","SPLIT",EDGE,{"disambiguationData":[TD([makeQuery(id+"F19.opExtrude","SWEPT_FACE",FACE,{"disambiguationData":[OSD([subQ0])]})])],"derivedFrom":makeQuery(id+"F1.opRevolve","SWEPT_EDGE",EDGE,{"disambiguationData":[OSD([subQ5,subQ3])]})});}
            var Q3;
            {var subQ0=sQuery(id+"F15.wireOp",EDGE,"E35");Q3=makeQuery(id+"F19.boolean.opBoolean","SPLIT",EDGE,{"disambiguationData":[TD([makeQuery(id+"F19.opExtrude","SWEPT_FACE",FACE,{"disambiguationData":[OSD([sQuery(id+"F17.wireOp",EDGE,"E46.1.0")])]})])],"derivedFrom":makeQuery(id+"F16.boolean.opBoolean","COPY",EDGE,{"derivedFrom":makeQuery(id+"F16.opExtrude","CAP_EDGE",EDGE,{"disambiguationData":[OSD([subQ0])],"isStart":false})})});}
            var Q4;
            {var subQ0=sQuery(id+"F15.wireOp",EDGE,"E35");Q4=makeQuery(id+"F19.boolean.opBoolean","SPLIT",EDGE,{"disambiguationData":[TD([makeQuery(id+"F19.opExtrude","SWEPT_FACE",FACE,{"disambiguationData":[OSD([sQuery(id+"F17.wireOp",EDGE,"E45.MirrorCS")])]})])],"derivedFrom":makeQuery(id+"F16.boolean.opBoolean","COPY",EDGE,{"derivedFrom":makeQuery(id+"F16.opExtrude","CAP_EDGE",EDGE,{"disambiguationData":[OSD([subQ0])],"isStart":false})})});}
            var Q5;
            {var subQ0=sQuery(id+"F15.wireOp",EDGE,"E35");Q5=makeQuery(id+"F19.boolean.opBoolean","SPLIT",EDGE,{"disambiguationData":[TD([makeQuery(id+"F19.opExtrude","SWEPT_FACE",FACE,{"disambiguationData":[OSD([sQuery(id+"F17.wireOp",EDGE,"E44")])]})])],"derivedFrom":makeQuery(id+"F16.boolean.opBoolean","COPY",EDGE,{"derivedFrom":makeQuery(id+"F16.opExtrude","CAP_EDGE",EDGE,{"disambiguationData":[OSD([subQ0])],"isStart":false})})});}
            fillet(context, id + "F20", {"entities" : qUnion([Q0, Q1, Q2, Q3, Q4, Q5]), "radius" : .2 * mm, "tangentPropagation" : true, "allowEdgeOverflow" : false});
        }
        {
            var Q0;
            {var subQ0=sQuery(id+"F17.wireOp",EDGE,"E42");var subQ1=sQuery(id+"F17.wireOp",EDGE,"E41");Q0=makeQuery(id+"F19.boolean.opBoolean","MERGE",FACE,{"derivedFrom":[makeQuery(id+"F1.opRevolve","SWEPT_FACE",FACE,{"disambiguationData":[OSD([sQuery(id+"F0.wireOp",EDGE,"E7")])]}),makeQuery(id+"F19.opExtrude","CAP_FACE",FACE,{"disambiguationData":[OSD([subQ1,subQ0,sQuery(id+"F17.wireOp",EDGE,"E44"),sQuery(id+"F17.wireOp",EDGE,"E45.MirrorCS")])],"isStart":true}),makeQuery(id+"F19.opExtrude","CAP_FACE",FACE,{"disambiguationData":[OSD([subQ1,subQ0,sQuery(id+"F17.wireOp",EDGE,"E46.1.0"),sQuery(id+"F17.wireOp",EDGE,"E46.1.1")])],"isStart":true}),makeQuery(id+"F19.opExtrude","CAP_FACE",FACE,{"disambiguationData":[OSD([subQ1,subQ0,sQuery(id+"F17.wireOp",EDGE,"E46.2.0"),sQuery(id+"F17.wireOp",EDGE,"E46.2.1")])],"isStart":true})]});}
            var sketch = newSketch(context, id + "F21", { "sketchPlane" : qUnion([Q0])});
            skLineSegment(sketch, "E47", {"start": v(0, 127.93) * mm, "end": v(0, 0) * mm, "construction": true});
            skLineSegment(sketch, "E48", {"start": v(0, 0) * mm, "end": v(-170.85, 0) * mm, "construction": true});
            skCircle(sketch, "E49", {"center": v(0, 0) * mm, "radius": 34.9 * mm});
            skArc(sketch, "E50", {"start": v(-1, 34.89) * mm, "mid": v(0, 33.9) * mm, "end": v(1, 34.89) * mm});
            skArc(sketch, "E51.1.0", {"start": v(-29.7, -18.31) * mm, "mid": v(-29.35, -16.95) * mm, "end": v(-30.71, -16.57) * mm});
            skArc(sketch, "E51.2.0", {"start": v(30.71, -16.57) * mm, "mid": v(29.35, -16.95) * mm, "end": v(29.7, -18.31) * mm});
            skSolve(sketch);
        }
        {
            var Q0;
            {var subQ0=sQuery(id+"F21.wireOp",EDGE,"E51.1.0");Q0=makeQuery(id+"F21.imprint","IMPRINT",FACE,{"disambiguationData":[TD([[makeQuery(id+"F21.imprint","IMPRINT",EDGE,{"derivedFrom":subQ0}),1.0]])]});}
            var Q1;
            {var subQ0=sQuery(id+"F21.wireOp",EDGE,"E51.2.0");Q1=makeQuery(id+"F21.imprint","IMPRINT",FACE,{"disambiguationData":[TD([[makeQuery(id+"F21.imprint","IMPRINT",EDGE,{"derivedFrom":subQ0}),1.0]])]});}
            var Q2;
            {var subQ0=sQuery(id+"F21.wireOp",EDGE,"E50");Q2=makeQuery(id+"F21.imprint","IMPRINT",FACE,{"disambiguationData":[TD([[makeQuery(id+"F21.imprint","IMPRINT",EDGE,{"derivedFrom":subQ0}),1.0]])]});}
            extrude(context, id + "F22", {"entities" : qUnion([Q0, Q1, Q2]), "depth" : 1.5 * mm, "offsetDistance" : 25 * mm});
        }
        {
            var Q0;
            Q0=makeQuery(id+"F1.opRevolve","SWEPT_FACE",FACE,{"disambiguationData":[OSD([sQuery(id+"F0.wireOp",EDGE,"E2.top"),sQuery(id+"F0.wireOp",EDGE,"E12")])]});
            var sketch = newSketch(context, id + "F23", { "sketchPlane" : qUnion([Q0])});
            skCircle(sketch, "E52", {"center": v(0, 0) * mm, "radius": 35.3 * mm});
            skArc(sketch, "E53", {"start": v(4.14, 35.46) * mm, "mid": v(-28.08, 22.05) * mm, "end": v(-33.47, -12.43) * mm});
            skLineSegment(sketch, "E54", {"start": v(0, 77.91) * mm, "end": v(0, 0) * mm, "construction": true});
            skArc(sketch, "E55", {"start": v(5.99, 34.79) * mm, "mid": v(5.14, 35.93) * mm, "end": v(4, 35.07) * mm});
            skArc(sketch, "E56.1.0", {"start": v(-33.12, -12.2) * mm, "mid": v(-33.7, -13.51) * mm, "end": v(-32.38, -14.06) * mm});
            skArc(sketch, "E56.2.0", {"start": v(27.13, -22.58) * mm, "mid": v(28.55, -22.42) * mm, "end": v(28.37, -21) * mm});
            skArc(sketch, "E57.trimOffspring", {"start": v(28.64, -21.32) * mm, "mid": v(33.13, 13.3) * mm, "end": v(5.97, 35.2) * mm});
            skArc(sketch, "E58.trimOffspring", {"start": v(-32.78, -14.14) * mm, "mid": v(-5.06, -35.34) * mm, "end": v(27.5, -22.77) * mm});
            skSolve(sketch);
        }
        {
            var Q0;
            {var subQ0=sQuery(id+"F23.wireOp",EDGE,"E55");var subQ1=sQuery(id+"F23.wireOp",EDGE,"E52");var subQ2=makeQuery(id+"F23.imprint","INTERSECT",VERTEX,{"disambiguationData":[OD(0.0)],"derivedFrom":[subQ1,subQ0]});Q0=makeQuery(id+"F23.imprint","IMPRINT",FACE,{"disambiguationData":[TD([[makeQuery(id+"F23.imprint","IMPRINT",EDGE,{"disambiguationData":[TD([[subQ2,-1.0]])],"derivedFrom":subQ1}),-1.0]])]});}
            var Q1;
            {var subQ0=sQuery(id+"F23.wireOp",EDGE,"E56.2.0");var subQ1=sQuery(id+"F23.wireOp",EDGE,"E52");var subQ2=makeQuery(id+"F23.imprint","INTERSECT",VERTEX,{"disambiguationData":[OD(0.0)],"derivedFrom":[subQ1,subQ0]});Q1=makeQuery(id+"F23.imprint","IMPRINT",FACE,{"disambiguationData":[TD([[makeQuery(id+"F23.imprint","IMPRINT",EDGE,{"disambiguationData":[TD([[subQ2,-1.0]])],"derivedFrom":subQ1}),-1.0]])]});}
            var Q2;
            {var subQ0=sQuery(id+"F23.wireOp",EDGE,"E56.1.0");var subQ1=sQuery(id+"F23.wireOp",EDGE,"E52");var subQ2=makeQuery(id+"F23.imprint","INTERSECT",VERTEX,{"disambiguationData":[OD(0.0)],"derivedFrom":[subQ1,subQ0]});Q2=makeQuery(id+"F23.imprint","IMPRINT",FACE,{"disambiguationData":[TD([[makeQuery(id+"F23.imprint","IMPRINT",EDGE,{"disambiguationData":[TD([[subQ2,-1.0]])],"derivedFrom":subQ1}),-1.0]])]});}
            extrude(context, id + "F24", {"entities" : qUnion([Q0, Q1, Q2]), "operationType" : NewBodyOperationType.REMOVE, "oppositeDirection" : true, "depth" : .5 * mm, "offsetDistance" : 25 * mm});
        }
    });
